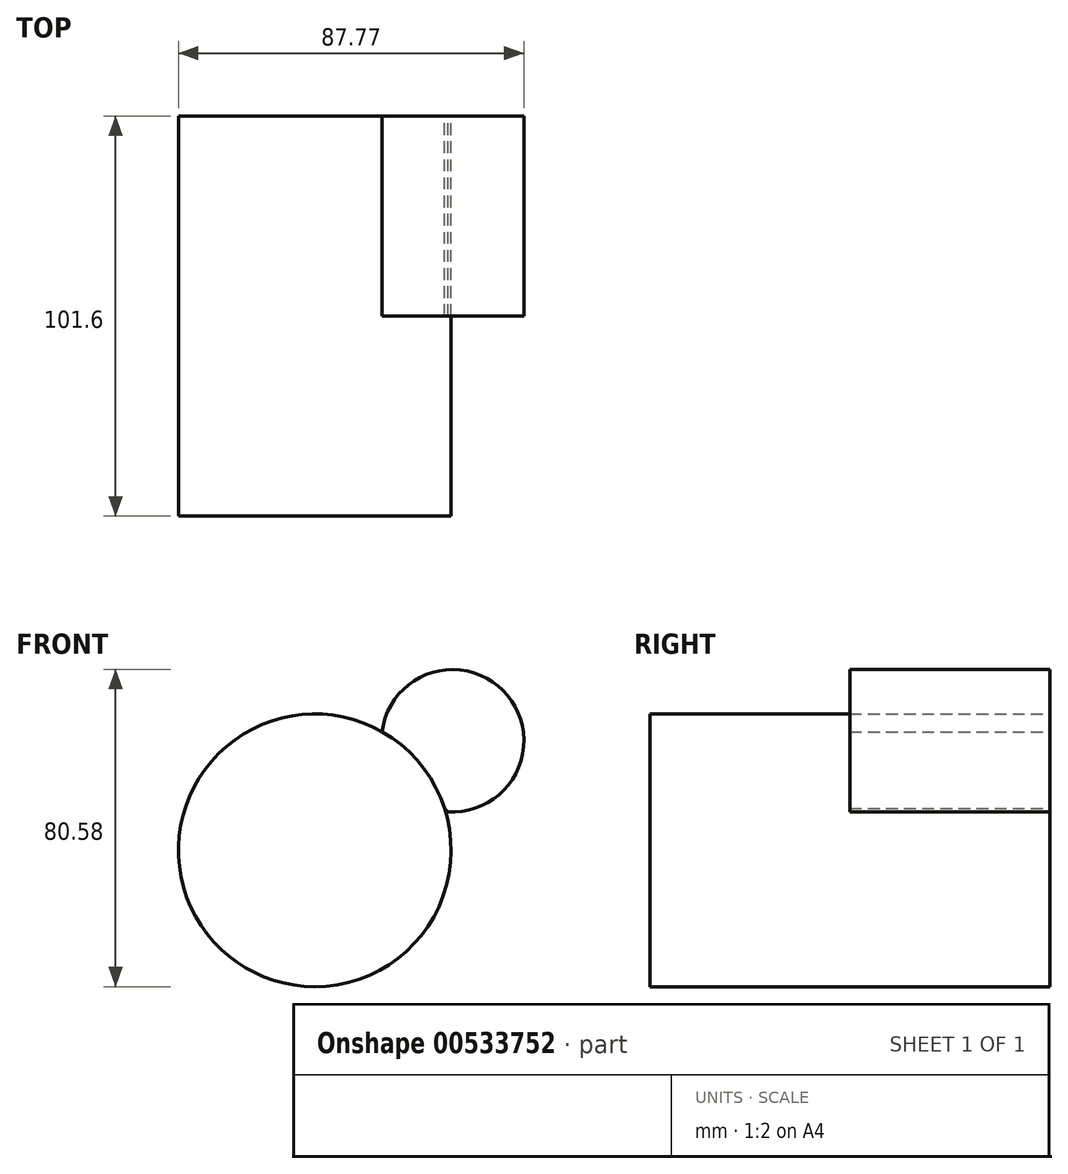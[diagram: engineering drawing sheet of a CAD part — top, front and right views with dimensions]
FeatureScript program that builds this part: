
annotation { "Feature Type Name" : "Feature", "Feature Type Description" : "" }
export const myFeature = defineFeature(function(context is Context, id is Id, definition is map)
    precondition{}
    {
        {
            var Q0;
            Q0=qCreatedBy(makeId("Front.planeOp"),FACE);
            var sketch = newSketch(context, id + "F0", { "sketchPlane" : qUnion([Q0])});
            skCircle(sketch, "E0", {"center": v(0, 0) * mm, "radius": 34.64 * mm});
            skSolve(sketch);
        }
        {
            var Q0;
            Q0 = qSketchRegion(id + "F0", true);
            extrude(context, id + "F1", {"entities" : qUnion([Q0]), "depth" : 50.8 * mm, "offsetDistance" : 25.4 * mm});
        }
        {
            var Q0;
            Q0=makeQuery(id+"F1.opExtrude","CAP_FACE",FACE,{"disambiguationData":[OSD([sQuery(id+"F0.wireOp",EDGE,"E0")])],"isStart":false});
            extrude(context, id + "F2", {"entities" : qUnion([Q0]), "operationType" : NewBodyOperationType.ADD, "depth" : 50.8 * mm, "offsetDistance" : 25.4 * mm});
        }
        {
            var Q0;
            Q0=qCreatedBy(makeId("Front.planeOp"),FACE);
            var sketch = newSketch(context, id + "F3", { "sketchPlane" : qUnion([Q0])});
            skArc(sketch, "E1", {"start": v(33.85, 9.8) * mm, "mid": v(47.5, 40.96) * mm, "end": v(17.07, 25.74) * mm});
            skLineSegment(sketch, "E2", {"start": v(17.07, 25.74) * mm, "end": v(33.85, 9.8) * mm});
            skSolve(sketch);
        }
        {
            var Q0;
            Q0 = qSketchRegion(id + "F3", true);
            extrude(context, id + "F4", {"entities" : qUnion([Q0]), "operationType" : NewBodyOperationType.ADD, "depth" : 25.4 * mm, "offsetDistance" : 25.4 * mm});
        }
        {
            var Q0;
            Q0=makeQuery(id+"F4.boolean.opBoolean","MERGE",FACE,{"derivedFrom":[makeQuery(id+"F1.opExtrude","CAP_FACE",FACE,{"disambiguationData":[OSD([sQuery(id+"F0.wireOp",EDGE,"E0")])],"isStart":true}),makeQuery(id+"F4.opExtrude","CAP_FACE",FACE,{"disambiguationData":[OSD([sQuery(id+"F3.wireOp",EDGE,"E1"),sQuery(id+"F3.wireOp",EDGE,"E2")])],"isStart":true})]});
            extrude(context, id + "F5", {"entities" : qUnion([Q0]), "operationType" : NewBodyOperationType.ADD, "depth" : -50.8 * mm, "offsetDistance" : 25.4 * mm});
        }
        {
            var Q0;
            Q0=makeQuery(id+"F4.boolean.opBoolean","MERGE",FACE,{"derivedFrom":[makeQuery(id+"F1.opExtrude","CAP_FACE",FACE,{"disambiguationData":[OSD([sQuery(id+"F0.wireOp",EDGE,"E0")])],"isStart":true}),makeQuery(id+"F4.opExtrude","CAP_FACE",FACE,{"disambiguationData":[OSD([sQuery(id+"F3.wireOp",EDGE,"E1"),sQuery(id+"F3.wireOp",EDGE,"E2")])],"isStart":true})]});
            extrude(context, id + "F6", {"entities" : qUnion([Q0]), "operationType" : NewBodyOperationType.ADD, "depth" : -25.4 * mm, "offsetDistance" : 25.4 * mm});
        }
        {
            var Q0;
            Q0=qCreatedBy(makeId("Front.planeOp"),FACE);
            var sketch = newSketch(context, id + "F7", { "sketchPlane" : qUnion([Q0])});
            skCircle(sketch, "E3", {"center": v(0, 0) * mm, "radius": 26.52 * mm});
            skSolve(sketch);
        }
        {
            var Q0;
            Q0 = qSketchRegion(id + "F7", true);
            extrude(context, id + "F8", {"entities" : qUnion([Q0]), "operationType" : NewBodyOperationType.REMOVE, "oppositeDirection" : true, "depth" : 25.4 * mm, "offsetDistance" : 25.4 * mm});
        }
        {
            var Q0;
            Q0=qCreatedBy(makeId("Front.planeOp"),FACE);
            var sketch = newSketch(context, id + "F9", { "sketchPlane" : qUnion([Q0])});
            skCircle(sketch, "E4", {"center": v(0, 0) * mm, "radius": 25.4 * mm});
            skSolve(sketch);
        }
        {
            var Q0;
            Q0=makeQuery(id+"F9.imprint","IMPRINT",FACE,{"disambiguationData":[TD([[makeQuery(id+"F9.imprint","IMPRINT",EDGE,{"derivedFrom":sQuery(id+"F9.wireOp",EDGE,"E4")}),1.0]])]});
            extrude(context, id + "F10", {"entities" : qUnion([Q0]), "operationType" : NewBodyOperationType.REMOVE, "oppositeDirection" : true, "depth" : 25.4 * mm, "offsetDistance" : 25.4 * mm});
        }
    });
